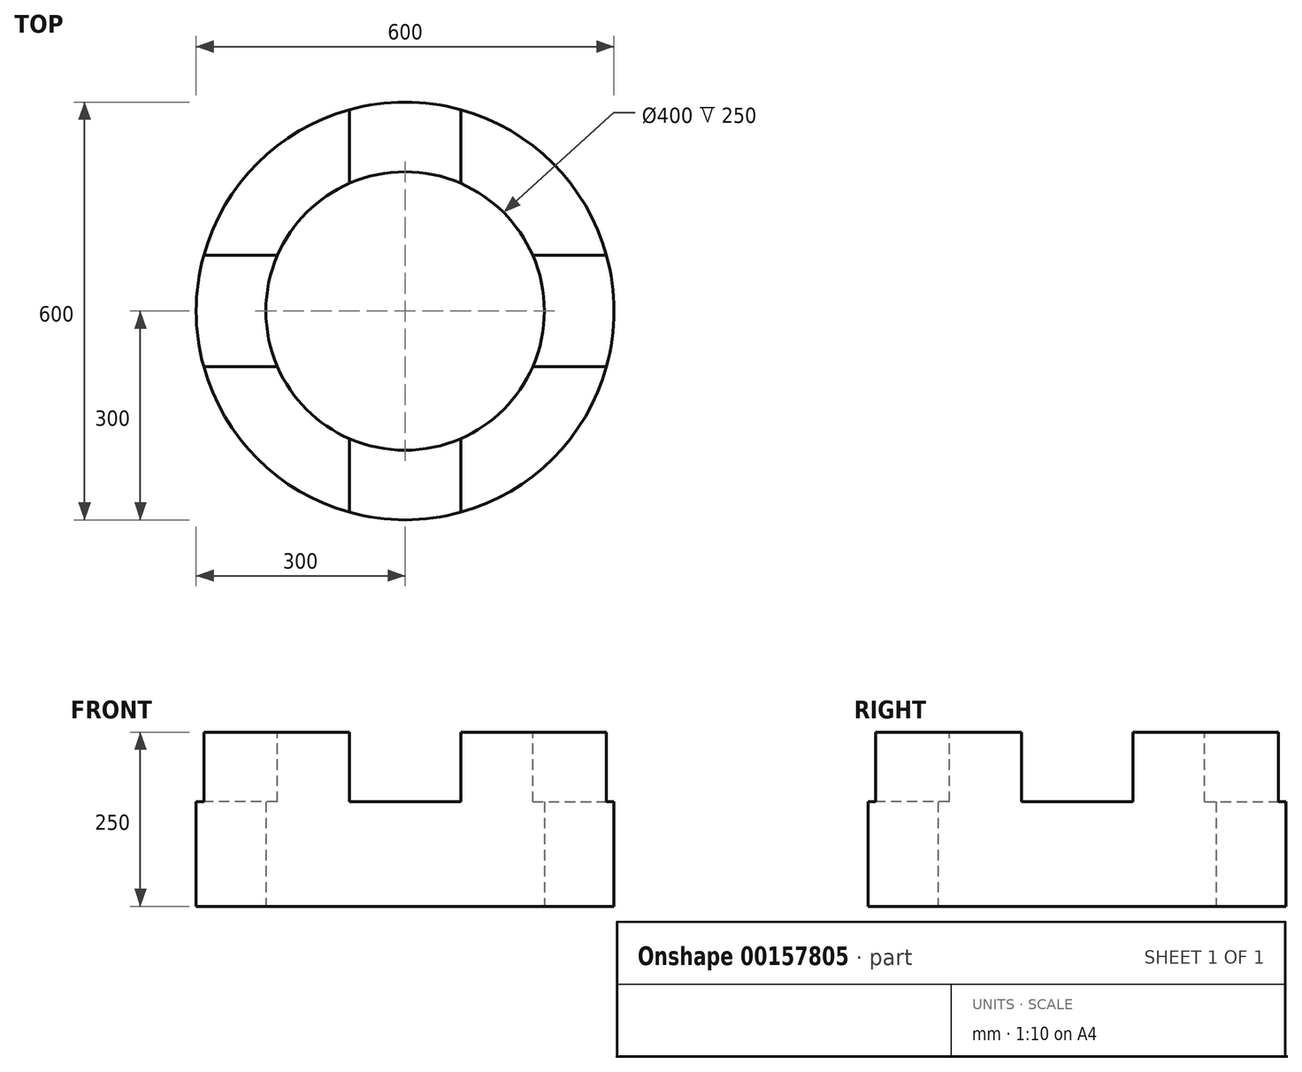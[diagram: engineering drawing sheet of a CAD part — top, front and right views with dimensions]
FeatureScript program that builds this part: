
annotation { "Feature Type Name" : "Feature", "Feature Type Description" : "" }
export const myFeature = defineFeature(function(context is Context, id is Id, definition is map)
    precondition{}
    {
        {
            var Q0;
            Q0=qCreatedBy(makeId("Top.planeOp"),FACE);
            var sketch = newSketch(context, id + "F0", { "sketchPlane" : qUnion([Q0])});
            skCircle(sketch, "E0", {"center": v(0, 0) * mm, "radius": 300 * mm});
            skCircle(sketch, "E1", {"center": v(0, 0) * mm, "radius": 200 * mm});
            skSolve(sketch);
        }
        {
            var Q0;
            Q0=makeQuery(id+"F0.imprint","IMPRINT",FACE,{"disambiguationData":[TD([[makeQuery(id+"F0.imprint","IMPRINT",EDGE,{"derivedFrom":sQuery(id+"F0.wireOp",EDGE,"E0")}),1.0]])]});
            extrude(context, id + "F1", {"entities" : qUnion([Q0]), "depth" : 250 * mm});
        }
        {
            var Q0;
            Q0=makeQuery(id+"F1.opExtrude","CAP_FACE",FACE,{"disambiguationData":[OSD([sQuery(id+"F0.wireOp",EDGE,"E0"),sQuery(id+"F0.wireOp",EDGE,"E1")])],"isStart":false});
            var sketch = newSketch(context, id + "F2", { "sketchPlane" : qUnion([Q0])});
            skLineSegment(sketch, "E2", {"start": v(0, 0) * mm, "end": v(0, 352.88) * mm, "construction": true});
            skLineSegment(sketch, "E3", {"start": v(0, 0) * mm, "end": v(407.8, 0) * mm, "construction": true});
            skLineSegment(sketch, "E4.0", {"start": v(80, 80) * mm, "end": v(80, 352.88) * mm});
            skLineSegment(sketch, "E5.0", {"start": v(80, 80) * mm, "end": v(407.8, 80) * mm});
            skLineSegment(sketch, "E6.MirrorCS", {"start": v(-80, 80) * mm, "end": v(-80, 352.88) * mm});
            skLineSegment(sketch, "E7.MirrorCS", {"start": v(80, -80) * mm, "end": v(407.8, -80) * mm});
            skLineSegment(sketch, "E8.MirrorCS", {"start": v(80, -80) * mm, "end": v(80, -352.88) * mm});
            skLineSegment(sketch, "E9.MirrorCS", {"start": v(-80, -80) * mm, "end": v(-80, -352.88) * mm});
            skLineSegment(sketch, "E10.MirrorCS", {"start": v(-80, 80) * mm, "end": v(-407.8, 80) * mm});
            skLineSegment(sketch, "E11.MirrorCS", {"start": v(-80, -80) * mm, "end": v(-407.8, -80) * mm});
            skPoint(sketch, "E12.orphan", {"position": v(0, 80) * mm});
            skPoint(sketch, "E13.orphan", {"position": v(80, 0) * mm});
            skPoint(sketch, "E14.orphan", {"position": v(0, -80) * mm});
            skPoint(sketch, "E15.orphan", {"position": v(-80, 0) * mm});
            skLineSegment(sketch, "E16", {"start": v(-80, 352.88) * mm, "end": v(80, 352.88) * mm});
            skLineSegment(sketch, "E17", {"start": v(407.8, 80) * mm, "end": v(407.8, -80) * mm});
            skLineSegment(sketch, "E18", {"start": v(80, -352.88) * mm, "end": v(-80, -352.88) * mm});
            skLineSegment(sketch, "E19", {"start": v(-407.8, -80) * mm, "end": v(-407.8, 80) * mm});
            skSolve(sketch);
        }
        {
            var Q0;
            {var subQ0=sQuery(id+"F2.wireOp",EDGE,"E4.0");var subQ1=makeQuery(id+"F1.opExtrude","CAP_EDGE",EDGE,{"disambiguationData":[OSD([sQuery(id+"F0.wireOp",EDGE,"E0")])],"isStart":false});var subQ2=makeQuery(id+"F2.imprint","INTERSECT",VERTEX,{"derivedFrom":[subQ1,subQ0]});Q0=makeQuery(id+"F2.imprint","IMPRINT",FACE,{"disambiguationData":[TD([[makeQuery(id+"F2.imprint","IMPRINT",EDGE,{"disambiguationData":[TD([[subQ2,1.0]])],"derivedFrom":subQ0}),1.0]])]});}
            var Q1;
            {var subQ0=sQuery(id+"F2.wireOp",EDGE,"E5.0");var subQ1=makeQuery(id+"F1.opExtrude","CAP_EDGE",EDGE,{"disambiguationData":[OSD([sQuery(id+"F0.wireOp",EDGE,"E0")])],"isStart":false});var subQ2=makeQuery(id+"F2.imprint","INTERSECT",VERTEX,{"derivedFrom":[subQ1,subQ0]});Q1=makeQuery(id+"F2.imprint","IMPRINT",FACE,{"disambiguationData":[TD([[makeQuery(id+"F2.imprint","IMPRINT",EDGE,{"disambiguationData":[TD([[subQ2,1.0]])],"derivedFrom":subQ0}),-1.0]])]});}
            var Q2;
            {var subQ0=sQuery(id+"F2.wireOp",EDGE,"E8.MirrorCS");var subQ1=makeQuery(id+"F1.opExtrude","CAP_EDGE",EDGE,{"disambiguationData":[OSD([sQuery(id+"F0.wireOp",EDGE,"E0")])],"isStart":false});var subQ2=makeQuery(id+"F2.imprint","INTERSECT",VERTEX,{"derivedFrom":[subQ1,subQ0]});Q2=makeQuery(id+"F2.imprint","IMPRINT",FACE,{"disambiguationData":[TD([[makeQuery(id+"F2.imprint","IMPRINT",EDGE,{"disambiguationData":[TD([[subQ2,1.0]])],"derivedFrom":subQ0}),-1.0]])]});}
            var Q3;
            {var subQ0=sQuery(id+"F2.wireOp",EDGE,"E10.MirrorCS");var subQ1=makeQuery(id+"F1.opExtrude","CAP_EDGE",EDGE,{"disambiguationData":[OSD([sQuery(id+"F0.wireOp",EDGE,"E0")])],"isStart":false});var subQ2=makeQuery(id+"F2.imprint","INTERSECT",VERTEX,{"derivedFrom":[subQ1,subQ0]});Q3=makeQuery(id+"F2.imprint","IMPRINT",FACE,{"disambiguationData":[TD([[makeQuery(id+"F2.imprint","IMPRINT",EDGE,{"disambiguationData":[TD([[subQ2,1.0]])],"derivedFrom":subQ0}),1.0]])]});}
            extrude(context, id + "F3", {"entities" : qUnion([Q0, Q1, Q2, Q3]), "operationType" : NewBodyOperationType.REMOVE, "oppositeDirection" : true, "depth" : 100 * mm});
        }
    });
